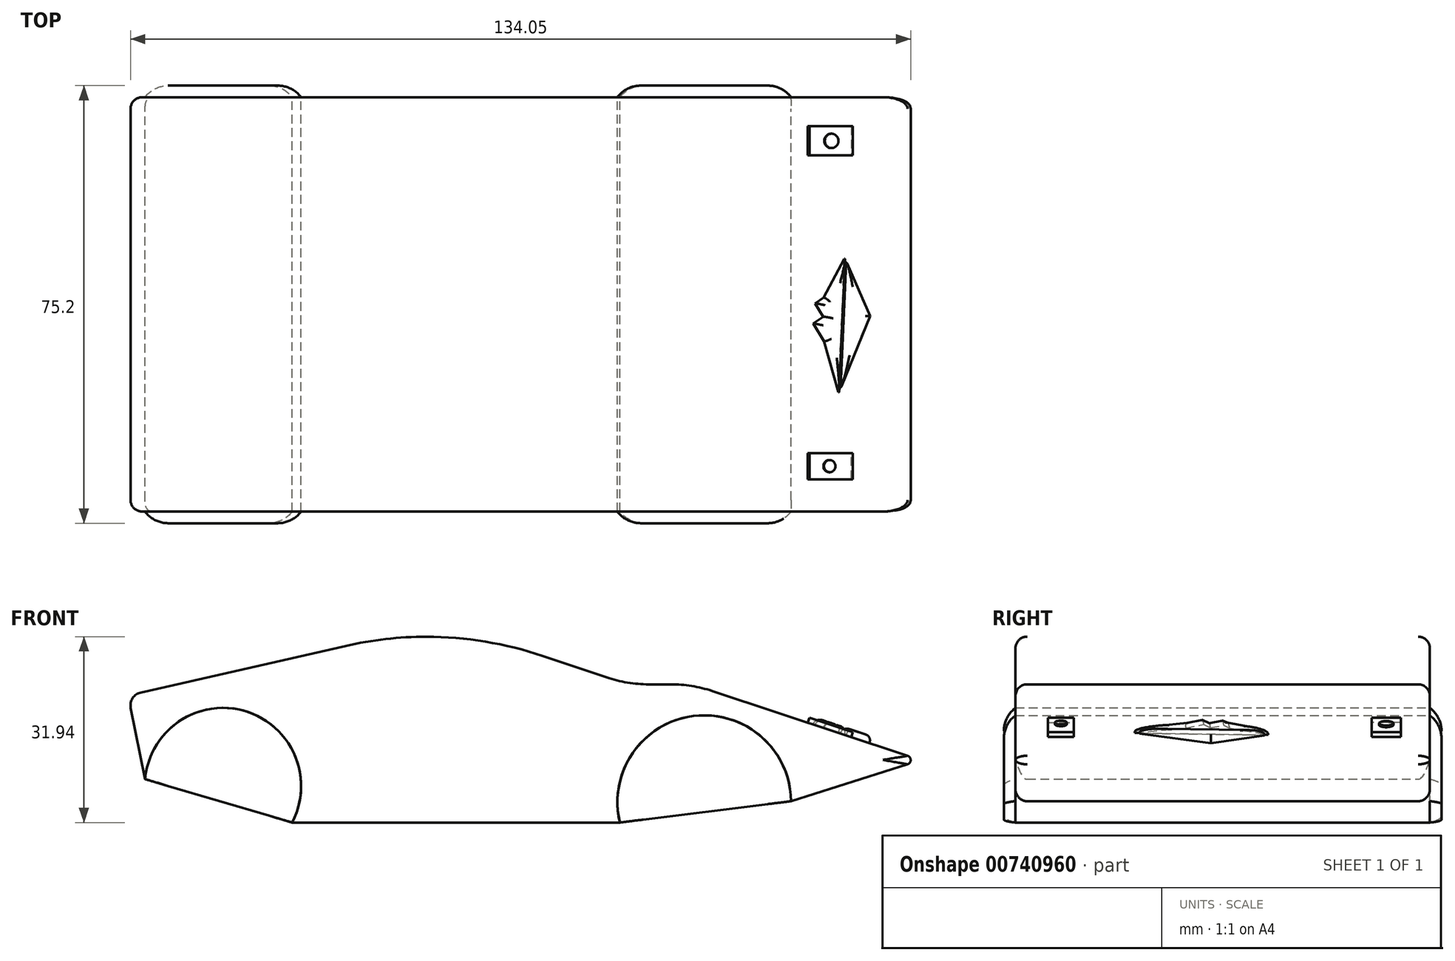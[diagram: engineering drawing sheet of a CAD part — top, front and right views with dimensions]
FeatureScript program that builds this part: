
annotation { "Feature Type Name" : "Feature", "Feature Type Description" : "" }
export const myFeature = defineFeature(function(context is Context, id is Id, definition is map)
    precondition{}
    {
        {
            var Q0;
            Q0=qCreatedBy(makeId("Front.planeOp"),FACE);
            var sketch = newSketch(context, id + "F0", { "sketchPlane" : qUnion([Q0])});
            skLineSegment(sketch, "E0.top", {"start": v(-38.49, -43.34) * mm, "end": v(17.83, -43.34) * mm});
            skLineSegment(sketch, "E1", {"start": v(69.52, -32.62) * mm, "end": v(47.24, -39.68) * mm});
            skLineSegment(sketch, "E2", {"start": v(17.83, -43.34) * mm, "end": v(-38.49, -43.34) * mm});
            skLineSegment(sketch, "E3", {"start": v(-62.76, -31.89) * mm, "end": v(-66.65, -21.48) * mm});
            skLineSegment(sketch, "E4", {"start": v(-66.65, -21.48) * mm, "end": v(-22.3, -11.4) * mm});
            skLineSegment(sketch, "E5", {"start": v(-22.3, -11.4) * mm, "end": v(-5.29, -11.4) * mm});
            skLineSegment(sketch, "E6", {"start": v(-5.29, -11.4) * mm, "end": v(19.09, -19.6) * mm});
            skLineSegment(sketch, "E7", {"start": v(19.09, -19.6) * mm, "end": v(30.22, -19.6) * mm});
            skLineSegment(sketch, "E8", {"start": v(30.22, -19.6) * mm, "end": v(69.52, -32.62) * mm});
            skArc(sketch, "E9", {"start": v(47.24, -39.68) * mm, "mid": v(30.48, -25.03) * mm, "end": v(17.83, -43.34) * mm});
            skPoint(sketch, "E10.orphan", {"position": v(46.82, -43.34) * mm});
            skPoint(sketch, "E11.orphan", {"position": v(35.69, -43.34) * mm});
            skArc(sketch, "E12", {"start": v(-38.49, -43.34) * mm, "mid": v(-50.37, -23.64) * mm, "end": v(-62.26, -43.34) * mm});
            skLineSegment(sketch, "E13", {"start": v(-66.65, -21.48) * mm, "end": v(-62.26, -43.34) * mm});
            skSolve(sketch);
        }
        {
            var Q0;
            Q0=makeQuery(id+"F0.imprint","IMPRINT",FACE,{"disambiguationData":[TD([[makeQuery(id+"F0.imprint","IMPRINT",EDGE,{"derivedFrom":sQuery(id+"F0.wireOp",EDGE,"E1")}),-1.0]])]});
            var Q1;
            {var subQ0=sQuery(id+"F0.wireOp",EDGE,"E3");Q1=makeQuery(id+"F0.imprint","IMPRINT",FACE,{"disambiguationData":[TD([[makeQuery(id+"F0.imprint","IMPRINT",EDGE,{"derivedFrom":subQ0}),1.0]])]});}
            extrude(context, id + "F1", {"entities" : qUnion([Q0, Q1]), "depth" : 71.2 * mm, "offsetDistance" : 25 * mm});
        }
        {
            var Q0;
            Q0=makeQuery(id+"F1.opExtrude","SWEPT_EDGE",EDGE,{"disambiguationData":[OSD([sQuery(id+"F0.wireOp",EDGE,"E1"),sQuery(id+"F0.wireOp",EDGE,"E8")])]});
            fillet(context, id + "F2", {"entities" : qUnion([Q0]), "radius" : 0.77 * mm, "tangentPropagation" : true, "allowEdgeOverflow" : false});
        }
        {
            var Q0;
            Q0=makeQuery(id+"F1.opExtrude","SWEPT_EDGE",EDGE,{"disambiguationData":[OSD([sQuery(id+"F0.wireOp",EDGE,"E7"),sQuery(id+"F0.wireOp",EDGE,"E8")])]});
            var Q1;
            Q1=makeQuery(id+"F1.opExtrude","SWEPT_EDGE",EDGE,{"disambiguationData":[OSD([sQuery(id+"F0.wireOp",EDGE,"E6"),sQuery(id+"F0.wireOp",EDGE,"E7")])]});
            fillet(context, id + "F3", {"entities" : qUnion([Q0, Q1]), "radius" : 22.57 * mm, "tangentPropagation" : true, "allowEdgeOverflow" : false});
        }
        {
            var Q0;
            Q0=makeQuery(id+"F1.opExtrude","SWEPT_EDGE",EDGE,{"disambiguationData":[OSD([sQuery(id+"F0.wireOp",EDGE,"E5"),sQuery(id+"F0.wireOp",EDGE,"E6")])]});
            var Q1;
            Q1=makeQuery(id+"F1.opExtrude","SWEPT_EDGE",EDGE,{"disambiguationData":[OSD([sQuery(id+"F0.wireOp",EDGE,"E4"),sQuery(id+"F0.wireOp",EDGE,"E5")])]});
            fillet(context, id + "F4", {"entities" : qUnion([Q0, Q1]), "radius" : 63.62 * mm, "tangentPropagation" : true, "allowEdgeOverflow" : false});
        }
        {
            var Q0;
            Q0=makeQuery(id+"F1.opExtrude","SWEPT_EDGE",EDGE,{"disambiguationData":[OSD([sQuery(id+"F0.wireOp",EDGE,"E3"),sQuery(id+"F0.wireOp",EDGE,"E4"),sQuery(id+"F0.wireOp",EDGE,"E13")])]});
            fillet(context, id + "F5", {"entities" : qUnion([Q0]), "radius" : 2.27 * mm, "tangentPropagation" : true, "allowEdgeOverflow" : false});
        }
        {
            var Q0;
            Q0=makeQuery(id+"F1.opExtrude","CAP_FACE",FACE,{"disambiguationData":[OSD([sQuery(id+"F0.wireOp",EDGE,"E1"),sQuery(id+"F0.wireOp",EDGE,"E2"),sQuery(id+"F0.wireOp",EDGE,"E4"),sQuery(id+"F0.wireOp",EDGE,"E5"),sQuery(id+"F0.wireOp",EDGE,"E6"),sQuery(id+"F0.wireOp",EDGE,"E7"),sQuery(id+"F0.wireOp",EDGE,"E8"),sQuery(id+"F0.wireOp",EDGE,"E9"),sQuery(id+"F0.wireOp",EDGE,"E12"),sQuery(id+"F0.wireOp",EDGE,"E13")])],"isStart":false});
            var sketch = newSketch(context, id + "F6", { "sketchPlane" : qUnion([Q0])});
            skLineSegment(sketch, "E14", {"start": v(17.83, -43.34) * mm, "end": v(47.24, -39.68) * mm});
            skSolve(sketch);
        }
        {
            var Q0;
            Q0=makeQuery(id+"F6.imprint","IMPRINT",FACE,{"disambiguationData":[TD([[makeQuery(id+"F6.imprint","IMPRINT",EDGE,{"derivedFrom":sQuery(id+"F6.wireOp",EDGE,"E14")}),1.0]])]});
            extrude(context, id + "F7", {"entities" : qUnion([Q0]), "depth" : 2 * mm, "offsetDistance" : 25 * mm});
        }
        {
            var Q0;
            Q0=makeQuery(id+"F1.opExtrude","CAP_FACE",FACE,{"disambiguationData":[OSD([sQuery(id+"F0.wireOp",EDGE,"E1"),sQuery(id+"F0.wireOp",EDGE,"E2"),sQuery(id+"F0.wireOp",EDGE,"E4"),sQuery(id+"F0.wireOp",EDGE,"E5"),sQuery(id+"F0.wireOp",EDGE,"E6"),sQuery(id+"F0.wireOp",EDGE,"E7"),sQuery(id+"F0.wireOp",EDGE,"E8"),sQuery(id+"F0.wireOp",EDGE,"E9"),sQuery(id+"F0.wireOp",EDGE,"E12"),sQuery(id+"F0.wireOp",EDGE,"E13")])],"isStart":true});
            var sketch = newSketch(context, id + "F8", { "sketchPlane" : qUnion([Q0])});
            skLineSegment(sketch, "E15", {"start": v(-47.24, -39.68) * mm, "end": v(-17.83, -43.34) * mm});
            skSolve(sketch);
        }
        {
            var Q0;
            Q0=makeQuery(id+"F8.imprint","IMPRINT",FACE,{"disambiguationData":[TD([[makeQuery(id+"F8.imprint","IMPRINT",EDGE,{"derivedFrom":sQuery(id+"F8.wireOp",EDGE,"E15")}),1.0]])]});
            extrude(context, id + "F9", {"entities" : qUnion([Q0]), "depth" : 2 * mm, "offsetDistance" : 25 * mm});
        }
        {
            var Q0;
            Q0=makeQuery(id+"F1.opExtrude","CAP_FACE",FACE,{"disambiguationData":[OSD([sQuery(id+"F0.wireOp",EDGE,"E1"),sQuery(id+"F0.wireOp",EDGE,"E2"),sQuery(id+"F0.wireOp",EDGE,"E4"),sQuery(id+"F0.wireOp",EDGE,"E5"),sQuery(id+"F0.wireOp",EDGE,"E6"),sQuery(id+"F0.wireOp",EDGE,"E7"),sQuery(id+"F0.wireOp",EDGE,"E8"),sQuery(id+"F0.wireOp",EDGE,"E9"),sQuery(id+"F0.wireOp",EDGE,"E12"),sQuery(id+"F0.wireOp",EDGE,"E13")])],"isStart":false});
            var sketch = newSketch(context, id + "F10", { "sketchPlane" : qUnion([Q0])});
            skLineSegment(sketch, "E16", {"start": v(-63.75, -35.89) * mm, "end": v(-38.49, -43.34) * mm});
            skSolve(sketch);
        }
        {
            var Q0;
            Q0=makeQuery(id+"F1.opExtrude","CAP_FACE",FACE,{"disambiguationData":[OSD([sQuery(id+"F0.wireOp",EDGE,"E1"),sQuery(id+"F0.wireOp",EDGE,"E2"),sQuery(id+"F0.wireOp",EDGE,"E4"),sQuery(id+"F0.wireOp",EDGE,"E5"),sQuery(id+"F0.wireOp",EDGE,"E6"),sQuery(id+"F0.wireOp",EDGE,"E7"),sQuery(id+"F0.wireOp",EDGE,"E8"),sQuery(id+"F0.wireOp",EDGE,"E9"),sQuery(id+"F0.wireOp",EDGE,"E12"),sQuery(id+"F0.wireOp",EDGE,"E13")])],"isStart":true});
            var sketch = newSketch(context, id + "F11", { "sketchPlane" : qUnion([Q0])});
            skLineSegment(sketch, "E17", {"start": v(38.49, -43.34) * mm, "end": v(63.75, -35.89) * mm});
            skSolve(sketch);
        }
        {
            var Q0;
            Q0=makeQuery(id+"F11.imprint","IMPRINT",FACE,{"disambiguationData":[TD([[makeQuery(id+"F11.imprint","IMPRINT",EDGE,{"derivedFrom":sQuery(id+"F11.wireOp",EDGE,"E17")}),1.0]])]});
            extrude(context, id + "F12", {"entities" : qUnion([Q0]), "depth" : 2 * mm, "offsetDistance" : 25 * mm});
        }
        {
            var Q0;
            Q0=makeQuery(id+"F10.imprint","IMPRINT",FACE,{"disambiguationData":[TD([[makeQuery(id+"F10.imprint","IMPRINT",EDGE,{"derivedFrom":sQuery(id+"F10.wireOp",EDGE,"E16")}),1.0]])]});
            extrude(context, id + "F13", {"entities" : qUnion([Q0]), "depth" : 2 * mm, "offsetDistance" : 25 * mm});
        }
        {
            var Q0;
            Q0=makeQuery(id+"F13.opExtrude","CAP_EDGE",EDGE,{"disambiguationData":[OSD([sQuery(id+"F0.wireOp",EDGE,"E12")])],"isStart":false});
            var Q1;
            Q1=makeQuery(id+"F7.opExtrude","CAP_EDGE",EDGE,{"disambiguationData":[OSD([sQuery(id+"F0.wireOp",EDGE,"E9")])],"isStart":false});
            var Q2;
            Q2=makeQuery(id+"F12.opExtrude","CAP_EDGE",EDGE,{"disambiguationData":[OSD([sQuery(id+"F0.wireOp",EDGE,"E12")])],"isStart":false});
            var Q3;
            Q3=makeQuery(id+"F9.opExtrude","CAP_EDGE",EDGE,{"disambiguationData":[OSD([sQuery(id+"F0.wireOp",EDGE,"E9")])],"isStart":false});
            fillet(context, id + "F14", {"entities" : qUnion([Q0, Q1, Q2, Q3]), "radius" : 5 * mm, "tangentPropagation" : true, "allowEdgeOverflow" : false});
        }
        {
            var Q0;
            Q0=makeQuery(id+"F1.opExtrude","CAP_EDGE",EDGE,{"disambiguationData":[OSD([sQuery(id+"F0.wireOp",EDGE,"E6")])],"isStart":false});
            var Q1;
            {var subQ0=sQuery(id+"F0.wireOp",EDGE,"E6");var subQ1=sQuery(id+"F0.wireOp",EDGE,"E5");Q1=makeQuery(id+"F4.opFillet","BLEND_EDGE",EDGE,{"blendedFrom":[makeQuery(id+"F1.opExtrude","SWEPT_EDGE",EDGE,{"disambiguationData":[OSD([subQ1,subQ0])]}),makeQuery(id+"F1.opExtrude","CAP_FACE",FACE,{"disambiguationData":[OSD([sQuery(id+"F0.wireOp",EDGE,"E1"),sQuery(id+"F0.wireOp",EDGE,"E2"),sQuery(id+"F0.wireOp",EDGE,"E4"),subQ1,subQ0,sQuery(id+"F0.wireOp",EDGE,"E7"),sQuery(id+"F0.wireOp",EDGE,"E8"),sQuery(id+"F0.wireOp",EDGE,"E9"),sQuery(id+"F0.wireOp",EDGE,"E12"),sQuery(id+"F0.wireOp",EDGE,"E13")])],"isStart":false})],"blendedInto":[makeQuery(id+"F1.opExtrude","CAP_FACE",FACE,{"disambiguationData":[OSD([sQuery(id+"F0.wireOp",EDGE,"E1"),sQuery(id+"F0.wireOp",EDGE,"E2"),sQuery(id+"F0.wireOp",EDGE,"E4"),subQ1,subQ0,sQuery(id+"F0.wireOp",EDGE,"E7"),sQuery(id+"F0.wireOp",EDGE,"E8"),sQuery(id+"F0.wireOp",EDGE,"E9"),sQuery(id+"F0.wireOp",EDGE,"E12"),sQuery(id+"F0.wireOp",EDGE,"E13")])],"isStart":false})]});}
            var Q2;
            {var subQ0=sQuery(id+"F0.wireOp",EDGE,"E5");var subQ1=sQuery(id+"F0.wireOp",EDGE,"E4");Q2=makeQuery(id+"F4.opFillet","BLEND_EDGE",EDGE,{"blendedFrom":[makeQuery(id+"F1.opExtrude","SWEPT_EDGE",EDGE,{"disambiguationData":[OSD([subQ1,subQ0])]}),makeQuery(id+"F1.opExtrude","CAP_FACE",FACE,{"disambiguationData":[OSD([sQuery(id+"F0.wireOp",EDGE,"E1"),sQuery(id+"F0.wireOp",EDGE,"E2"),subQ1,subQ0,sQuery(id+"F0.wireOp",EDGE,"E6"),sQuery(id+"F0.wireOp",EDGE,"E7"),sQuery(id+"F0.wireOp",EDGE,"E8"),sQuery(id+"F0.wireOp",EDGE,"E9"),sQuery(id+"F0.wireOp",EDGE,"E12"),sQuery(id+"F0.wireOp",EDGE,"E13")])],"isStart":false})],"blendedInto":[makeQuery(id+"F1.opExtrude","CAP_FACE",FACE,{"disambiguationData":[OSD([sQuery(id+"F0.wireOp",EDGE,"E1"),sQuery(id+"F0.wireOp",EDGE,"E2"),subQ1,subQ0,sQuery(id+"F0.wireOp",EDGE,"E6"),sQuery(id+"F0.wireOp",EDGE,"E7"),sQuery(id+"F0.wireOp",EDGE,"E8"),sQuery(id+"F0.wireOp",EDGE,"E9"),sQuery(id+"F0.wireOp",EDGE,"E12"),sQuery(id+"F0.wireOp",EDGE,"E13")])],"isStart":false})]});}
            fillet(context, id + "F15", {"entities" : qUnion([Q0, Q1, Q2]), "radius" : 2 * mm, "tangentPropagation" : true, "allowEdgeOverflow" : false});
        }
        {
            var Q0;
            {var subQ0=sQuery(id+"F0.wireOp",EDGE,"E6");var subQ1=sQuery(id+"F0.wireOp",EDGE,"E5");Q0=makeQuery(id+"F4.opFillet","BLEND_EDGE",EDGE,{"blendedFrom":[makeQuery(id+"F1.opExtrude","SWEPT_EDGE",EDGE,{"disambiguationData":[OSD([subQ1,subQ0])]}),makeQuery(id+"F1.opExtrude","CAP_FACE",FACE,{"disambiguationData":[OSD([sQuery(id+"F0.wireOp",EDGE,"E1"),sQuery(id+"F0.wireOp",EDGE,"E2"),sQuery(id+"F0.wireOp",EDGE,"E4"),subQ1,subQ0,sQuery(id+"F0.wireOp",EDGE,"E7"),sQuery(id+"F0.wireOp",EDGE,"E8"),sQuery(id+"F0.wireOp",EDGE,"E9"),sQuery(id+"F0.wireOp",EDGE,"E12"),sQuery(id+"F0.wireOp",EDGE,"E13")])],"isStart":true})],"blendedInto":[makeQuery(id+"F1.opExtrude","CAP_FACE",FACE,{"disambiguationData":[OSD([sQuery(id+"F0.wireOp",EDGE,"E1"),sQuery(id+"F0.wireOp",EDGE,"E2"),sQuery(id+"F0.wireOp",EDGE,"E4"),subQ1,subQ0,sQuery(id+"F0.wireOp",EDGE,"E7"),sQuery(id+"F0.wireOp",EDGE,"E8"),sQuery(id+"F0.wireOp",EDGE,"E9"),sQuery(id+"F0.wireOp",EDGE,"E12"),sQuery(id+"F0.wireOp",EDGE,"E13")])],"isStart":true})]});}
            var Q1;
            Q1=makeQuery(id+"F1.opExtrude","CAP_EDGE",EDGE,{"disambiguationData":[OSD([sQuery(id+"F0.wireOp",EDGE,"E4")])],"isStart":true});
            var Q2;
            {var subQ0=sQuery(id+"F0.wireOp",EDGE,"E5");var subQ1=sQuery(id+"F0.wireOp",EDGE,"E4");Q2=makeQuery(id+"F4.opFillet","BLEND_EDGE",EDGE,{"blendedFrom":[makeQuery(id+"F1.opExtrude","SWEPT_EDGE",EDGE,{"disambiguationData":[OSD([subQ1,subQ0])]}),makeQuery(id+"F1.opExtrude","CAP_FACE",FACE,{"disambiguationData":[OSD([sQuery(id+"F0.wireOp",EDGE,"E1"),sQuery(id+"F0.wireOp",EDGE,"E2"),subQ1,subQ0,sQuery(id+"F0.wireOp",EDGE,"E6"),sQuery(id+"F0.wireOp",EDGE,"E7"),sQuery(id+"F0.wireOp",EDGE,"E8"),sQuery(id+"F0.wireOp",EDGE,"E9"),sQuery(id+"F0.wireOp",EDGE,"E12"),sQuery(id+"F0.wireOp",EDGE,"E13")])],"isStart":true})],"blendedInto":[makeQuery(id+"F1.opExtrude","CAP_FACE",FACE,{"disambiguationData":[OSD([sQuery(id+"F0.wireOp",EDGE,"E1"),sQuery(id+"F0.wireOp",EDGE,"E2"),subQ1,subQ0,sQuery(id+"F0.wireOp",EDGE,"E6"),sQuery(id+"F0.wireOp",EDGE,"E7"),sQuery(id+"F0.wireOp",EDGE,"E8"),sQuery(id+"F0.wireOp",EDGE,"E9"),sQuery(id+"F0.wireOp",EDGE,"E12"),sQuery(id+"F0.wireOp",EDGE,"E13")])],"isStart":true})]});}
            fillet(context, id + "F16", {"entities" : qUnion([Q0, Q1, Q2]), "radius" : 2 * mm, "tangentPropagation" : true, "allowEdgeOverflow" : false});
        }
        {
            var Q0;
            Q0=makeQuery(id+"F1.opExtrude","SWEPT_FACE",FACE,{"disambiguationData":[OSD([sQuery(id+"F0.wireOp",EDGE,"E8")])]});
            var sketch = newSketch(context, id + "F17", { "sketchPlane" : qUnion([Q0])});
            skLineSegment(sketch, "E18.bottom", {"start": v(55.8, -65.65) * mm, "end": v(63.66, -65.65) * mm});
            skLineSegment(sketch, "E18.top", {"start": v(55.8, -61.18) * mm, "end": v(63.66, -61.18) * mm});
            skLineSegment(sketch, "E18.left", {"start": v(55.8, -65.65) * mm, "end": v(55.8, -61.18) * mm});
            skLineSegment(sketch, "E18.right", {"start": v(63.66, -65.65) * mm, "end": v(63.66, -61.18) * mm});
            skLineSegment(sketch, "E19.bottom", {"start": v(55.8, -4.99) * mm, "end": v(63.66, -4.99) * mm});
            skLineSegment(sketch, "E19.top", {"start": v(55.8, -10) * mm, "end": v(63.66, -10) * mm});
            skLineSegment(sketch, "E19.left", {"start": v(55.8, -4.99) * mm, "end": v(55.8, -10) * mm});
            skLineSegment(sketch, "E19.right", {"start": v(63.66, -4.99) * mm, "end": v(63.66, -10) * mm});
            skSolve(sketch);
        }
        {
            var Q0;
            Q0 = qSketchRegion(id + "F17", true);
            extrude(context, id + "F18", {"entities" : qUnion([Q0]), "operationType" : NewBodyOperationType.ADD, "oppositeDirection" : true, "depth" : 2.1 * mm, "offsetDistance" : 25 * mm});
        }
        {
            var Q0;
            Q0 = qSketchRegion(id + "F17", true);
            extrude(context, id + "F19", {"entities" : qUnion([Q0]), "operationType" : NewBodyOperationType.ADD, "depth" : 0.9 * mm, "offsetDistance" : 25 * mm});
        }
        {
            var Q0;
            Q0=makeQuery(id+"F19.opExtrude","CAP_FACE",FACE,{"disambiguationData":[OSD([sQuery(id+"F17.wireOp",EDGE,"E18.bottom"),sQuery(id+"F17.wireOp",EDGE,"E18.top"),sQuery(id+"F17.wireOp",EDGE,"E18.left"),sQuery(id+"F17.wireOp",EDGE,"E18.right")])],"isStart":false});
            var sketch = newSketch(context, id + "F20", { "sketchPlane" : qUnion([Q0])});
            skCircle(sketch, "E20", {"center": v(59.38, -63.4) * mm, "radius": 1.04 * mm});
            skCircle(sketch, "E21", {"center": v(59.73, -7.5) * mm, "radius": 1.23 * mm});
            skPoint(sketch, "E21.centerSnap0", {"position": v(59.73, -61.18) * mm});
            skSolve(sketch);
        }
        {
            var Q0;
            Q0=makeQuery(id+"F20.imprint","IMPRINT",FACE,{"disambiguationData":[TD([[makeQuery(id+"F20.imprint","IMPRINT",EDGE,{"derivedFrom":sQuery(id+"F20.wireOp",EDGE,"E20")}),1.0]])]});
            var Q1;
            Q1=makeQuery(id+"F20.imprint","IMPRINT",FACE,{"disambiguationData":[TD([[makeQuery(id+"F20.imprint","IMPRINT",EDGE,{"derivedFrom":sQuery(id+"F20.wireOp",EDGE,"E21")}),1.0]])]});
            extrude(context, id + "F21", {"entities" : qUnion([Q0, Q1]), "operationType" : NewBodyOperationType.ADD, "depth" : 0.3 * mm, "offsetDistance" : 25 * mm});
        }
        {
            var Q0;
            Q0=makeQuery(id+"F1.opExtrude","SWEPT_FACE",FACE,{"disambiguationData":[OSD([sQuery(id+"F0.wireOp",EDGE,"E8")])]});
            var sketch = newSketch(context, id + "F22", { "sketchPlane" : qUnion([Q0])});
            skLineSegment(sketch, "E22", {"start": v(61.38, -50.7) * mm, "end": v(58.77, -41.95) * mm});
            skLineSegment(sketch, "E23", {"start": v(58.77, -41.95) * mm, "end": v(56.8, -38.9) * mm});
            skLineSegment(sketch, "E24", {"start": v(56.8, -38.9) * mm, "end": v(58.63, -37.71) * mm});
            skLineSegment(sketch, "E25", {"start": v(58.63, -37.71) * mm, "end": v(57.16, -35.45) * mm});
            skLineSegment(sketch, "E26", {"start": v(57.16, -35.45) * mm, "end": v(58.68, -34.46) * mm});
            skLineSegment(sketch, "E27", {"start": v(58.68, -34.46) * mm, "end": v(62.45, -27.8) * mm});
            skLineSegment(sketch, "E28", {"start": v(62.73, -28.42) * mm, "end": v(66.95, -37.6) * mm});
            skLineSegment(sketch, "E29", {"start": v(66.95, -37.6) * mm, "end": v(61.73, -49.86) * mm});
            skLineSegment(sketch, "E30", {"start": v(61.38, -50.7) * mm, "end": v(62.45, -27.8) * mm});
            skLineSegment(sketch, "E31", {"start": v(62.73, -28.42) * mm, "end": v(61.73, -49.86) * mm});
            skSolve(sketch);
        }
        {
            var Q0;
            Q0=makeQuery(id+"F22.imprint","IMPRINT",FACE,{"disambiguationData":[TD([[makeQuery(id+"F22.imprint","IMPRINT",EDGE,{"derivedFrom":sQuery(id+"F22.wireOp",EDGE,"E22")}),-1.0]])]});
            var Q1;
            Q1=makeQuery(id+"F22.imprint","IMPRINT",FACE,{"disambiguationData":[TD([[makeQuery(id+"F22.imprint","IMPRINT",EDGE,{"derivedFrom":sQuery(id+"F22.wireOp",EDGE,"E28")}),-1.0]])]});
            extrude(context, id + "F23", {"entities" : qUnion([Q0, Q1]), "operationType" : NewBodyOperationType.ADD, "depth" : 1.2 * mm, "offsetDistance" : 25 * mm});
        }
        {
            var Q0;
            Q0=makeQuery(id+"F23.opExtrude","CAP_EDGE",EDGE,{"disambiguationData":[OSD([sQuery(id+"F22.wireOp",EDGE,"E29")])],"isStart":false});
            var Q1;
            Q1=makeQuery(id+"F23.opExtrude","CAP_EDGE",EDGE,{"disambiguationData":[OSD([sQuery(id+"F22.wireOp",EDGE,"E28")])],"isStart":false});
            var Q2;
            Q2=makeQuery(id+"F23.opExtrude","CAP_EDGE",EDGE,{"disambiguationData":[OSD([sQuery(id+"F22.wireOp",EDGE,"E31")])],"isStart":false});
            fillet(context, id + "F24", {"entities" : qUnion([Q0, Q1, Q2]), "radius" : 1 * mm, "tangentPropagation" : true, "allowEdgeOverflow" : false});
        }
        {
            var Q0;
            Q0=makeQuery(id+"F23.opExtrude","CAP_EDGE",EDGE,{"disambiguationData":[OSD([sQuery(id+"F22.wireOp",EDGE,"E25")])],"isStart":false});
            var Q1;
            Q1=makeQuery(id+"F23.opExtrude","CAP_EDGE",EDGE,{"disambiguationData":[OSD([sQuery(id+"F22.wireOp",EDGE,"E26")])],"isStart":false});
            var Q2;
            Q2=makeQuery(id+"F23.opExtrude","CAP_EDGE",EDGE,{"disambiguationData":[OSD([sQuery(id+"F22.wireOp",EDGE,"E27")])],"isStart":false});
            var Q3;
            Q3=makeQuery(id+"F23.opExtrude","CAP_EDGE",EDGE,{"disambiguationData":[OSD([sQuery(id+"F22.wireOp",EDGE,"E30")])],"isStart":false});
            var Q4;
            Q4=makeQuery(id+"F23.opExtrude","CAP_EDGE",EDGE,{"disambiguationData":[OSD([sQuery(id+"F22.wireOp",EDGE,"E22")])],"isStart":false});
            var Q5;
            Q5=makeQuery(id+"F23.opExtrude","CAP_EDGE",EDGE,{"disambiguationData":[OSD([sQuery(id+"F22.wireOp",EDGE,"E23")])],"isStart":false});
            var Q6;
            Q6=makeQuery(id+"F23.opExtrude","CAP_EDGE",EDGE,{"disambiguationData":[OSD([sQuery(id+"F22.wireOp",EDGE,"E24")])],"isStart":false});
            fillet(context, id + "F25", {"entities" : qUnion([Q0, Q1, Q2, Q3, Q4, Q5, Q6]), "radius" : 1 * mm, "tangentPropagation" : true, "allowEdgeOverflow" : false});
        }
    });
